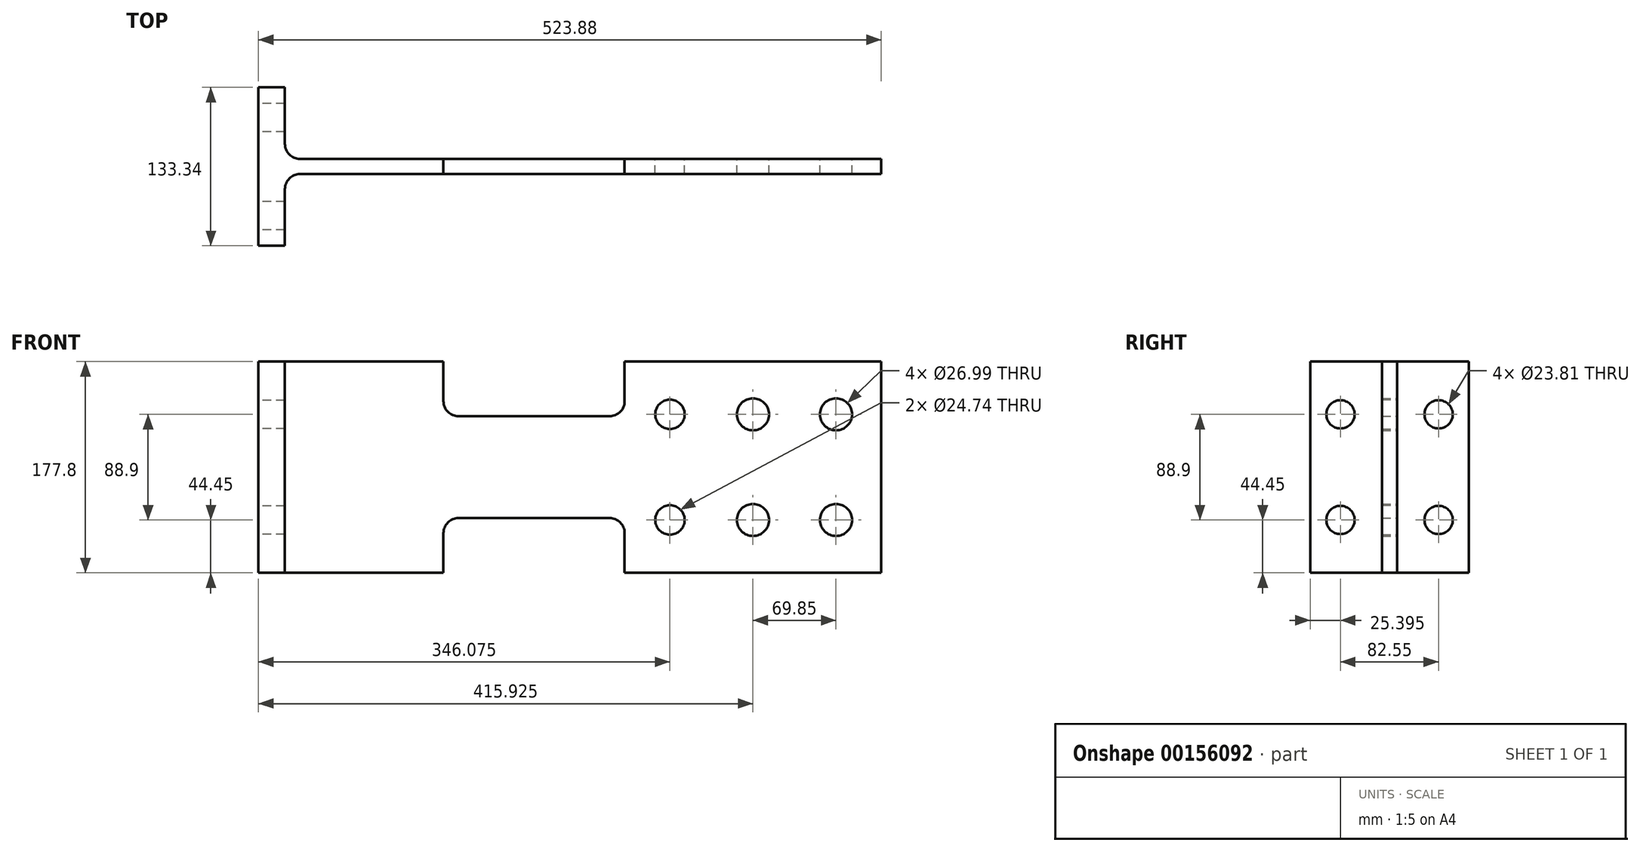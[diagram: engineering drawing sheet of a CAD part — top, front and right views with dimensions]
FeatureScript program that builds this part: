
annotation { "Feature Type Name" : "Feature", "Feature Type Description" : "" }
export const myFeature = defineFeature(function(context is Context, id is Id, definition is map)
    precondition{}
    {
        {
            var Q0;
            Q0=qCreatedBy(makeId("Front.planeOp"),FACE);
            var sketch = newSketch(context, id + "F0", { "sketchPlane" : qUnion([Q0])});
            skLineSegment(sketch, "E0", {"start": v(0, 0) * mm, "end": v(0, 88.9) * mm});
            skLineSegment(sketch, "E1", {"start": v(0, 88.9) * mm, "end": v(155.57, 88.9) * mm});
            skLineSegment(sketch, "E2", {"start": v(523.88, 88.9) * mm, "end": v(523.88, 0) * mm});
            skPoint(sketch, "E3", {"position": v(485.78, 44.45) * mm});
            skPoint(sketch, "E4", {"position": v(415.93, 44.45) * mm});
            skPoint(sketch, "E5", {"position": v(346.08, 44.45) * mm});
            skLineSegment(sketch, "E6", {"start": v(307.98, 88.9) * mm, "end": v(307.98, 55.56) * mm});
            skLineSegment(sketch, "E7", {"start": v(155.57, 88.9) * mm, "end": v(155.57, 55.56) * mm});
            skLineSegment(sketch, "E8", {"start": v(168.27, 42.86) * mm, "end": v(295.28, 42.86) * mm});
            skPoint(sketch, "E9.newPointA", {"position": v(155.57, 44.45) * mm});
            skArc(sketch, "E9.filletArc", {"start": v(155.57, 55.56) * mm, "mid": v(159.3, 46.58) * mm, "end": v(168.27, 42.86) * mm});
            skPoint(sketch, "E10.newPointA", {"position": v(307.98, 42.86) * mm});
            skPoint(sketch, "E10.newPointB", {"position": v(307.98, 44.45) * mm});
            skArc(sketch, "E10.filletArc", {"start": v(295.28, 42.86) * mm, "mid": v(304.26, 46.58) * mm, "end": v(307.98, 55.56) * mm});
            skCircle(sketch, "E11", {"center": v(346.08, 44.45) * mm, "radius": 12.37 * mm});
            skCircle(sketch, "E12", {"center": v(415.93, 44.45) * mm, "radius": 13.5 * mm});
            skCircle(sketch, "E13", {"center": v(485.78, 44.45) * mm, "radius": 13.5 * mm});
            skLineSegment(sketch, "E14.trimOffspring", {"start": v(307.98, 88.9) * mm, "end": v(523.88, 88.9) * mm});
            skArc(sketch, "E15.MirrorCS", {"start": v(155.57, -55.56) * mm, "mid": v(159.3, -46.58) * mm, "end": v(168.27, -42.86) * mm});
            skArc(sketch, "E16.MirrorCS", {"start": v(295.28, -42.86) * mm, "mid": v(304.26, -46.58) * mm, "end": v(307.98, -55.56) * mm});
            skPoint(sketch, "E17.MirrorP", {"position": v(307.98, -44.45) * mm});
            skPoint(sketch, "E18.MirrorP", {"position": v(307.98, -42.86) * mm});
            skLineSegment(sketch, "E19.MirrorCS", {"start": v(0, 0) * mm, "end": v(0, -88.9) * mm});
            skLineSegment(sketch, "E20.MirrorCS", {"start": v(0, -88.9) * mm, "end": v(155.57, -88.9) * mm});
            skLineSegment(sketch, "E21.MirrorCS", {"start": v(307.98, -88.9) * mm, "end": v(523.88, -88.9) * mm});
            skCircle(sketch, "E22.MirrorC", {"center": v(485.78, -44.45) * mm, "radius": 13.5 * mm});
            skLineSegment(sketch, "E23.MirrorCS", {"start": v(168.27, -42.86) * mm, "end": v(295.28, -42.86) * mm});
            skLineSegment(sketch, "E24.MirrorCS", {"start": v(523.88, -88.9) * mm, "end": v(523.88, 0) * mm});
            skPoint(sketch, "E25.MirrorP", {"position": v(155.57, -44.45) * mm});
            skCircle(sketch, "E26.MirrorC", {"center": v(346.08, -44.45) * mm, "radius": 12.37 * mm});
            skCircle(sketch, "E27.MirrorC", {"center": v(415.93, -44.45) * mm, "radius": 13.5 * mm});
            skLineSegment(sketch, "E28.MirrorCS", {"start": v(155.57, -88.9) * mm, "end": v(155.57, -55.56) * mm});
            skLineSegment(sketch, "E29.MirrorCS", {"start": v(307.98, -88.9) * mm, "end": v(307.98, -55.56) * mm});
            skSolve(sketch);
        }
        {
            var Q0;
            Q0=makeQuery(id+"F0.imprint","IMPRINT",FACE,{"disambiguationData":[TD([[makeQuery(id+"F0.imprint","IMPRINT",EDGE,{"derivedFrom":sQuery(id+"F0.wireOp",EDGE,"E0")}),-1.0]])]});
            extrude(context, id + "F1", {"entities" : qUnion([Q0]), "depth" : 6.35 * mm});
        }
        {
            var Q0;
            Q0=makeQuery(id+"F1.opExtrude","CAP_FACE",FACE,{"disambiguationData":[OSD([sQuery(id+"F0.wireOp",EDGE,"E0"),sQuery(id+"F0.wireOp",EDGE,"E1"),sQuery(id+"F0.wireOp",EDGE,"E2"),sQuery(id+"F0.wireOp",EDGE,"E6"),sQuery(id+"F0.wireOp",EDGE,"E7"),sQuery(id+"F0.wireOp",EDGE,"E8"),sQuery(id+"F0.wireOp",EDGE,"E9.filletArc"),sQuery(id+"F0.wireOp",EDGE,"E10.filletArc"),sQuery(id+"F0.wireOp",EDGE,"E11"),sQuery(id+"F0.wireOp",EDGE,"E12"),sQuery(id+"F0.wireOp",EDGE,"E13"),sQuery(id+"F0.wireOp",EDGE,"E14.trimOffspring"),sQuery(id+"F0.wireOp",EDGE,"E15.MirrorCS"),sQuery(id+"F0.wireOp",EDGE,"E16.MirrorCS"),sQuery(id+"F0.wireOp",EDGE,"E19.MirrorCS"),sQuery(id+"F0.wireOp",EDGE,"E20.MirrorCS"),sQuery(id+"F0.wireOp",EDGE,"E21.MirrorCS"),sQuery(id+"F0.wireOp",EDGE,"E22.MirrorC"),sQuery(id+"F0.wireOp",EDGE,"E23.MirrorCS"),sQuery(id+"F0.wireOp",EDGE,"E24.MirrorCS"),sQuery(id+"F0.wireOp",EDGE,"E26.MirrorC"),sQuery(id+"F0.wireOp",EDGE,"E27.MirrorC"),sQuery(id+"F0.wireOp",EDGE,"E28.MirrorCS"),sQuery(id+"F0.wireOp",EDGE,"E29.MirrorCS")])],"isStart":true});
            extrude(context, id + "F2", {"entities" : qUnion([Q0]), "operationType" : NewBodyOperationType.ADD, "depth" : 6.35 * mm});
        }
        {
            var Q0;
            Q0=qCreatedBy(makeId("Right.planeOp"),FACE);
            var sketch = newSketch(context, id + "F3", { "sketchPlane" : qUnion([Q0])});
            skLineSegment(sketch, "E30", {"start": v(0, 88.9) * mm, "end": v(-66.68, 88.9) * mm});
            skLineSegment(sketch, "E31", {"start": v(-66.68, 88.9) * mm, "end": v(-66.68, 0) * mm});
            skPoint(sketch, "E32", {"position": v(-66.68, 44.45) * mm});
            skPoint(sketch, "E33", {"position": v(-41.28, 44.45) * mm});
            skCircle(sketch, "E34", {"center": v(-41.28, 44.45) * mm, "radius": 11.9 * mm});
            skLineSegment(sketch, "E35.MirrorCS", {"start": v(0, 88.9) * mm, "end": v(66.68, 88.9) * mm});
            skLineSegment(sketch, "E36.MirrorCS", {"start": v(66.68, 88.9) * mm, "end": v(66.68, 0) * mm});
            skPoint(sketch, "E37.MirrorP", {"position": v(41.28, 44.45) * mm});
            skPoint(sketch, "E38.MirrorP", {"position": v(66.68, 44.45) * mm});
            skCircle(sketch, "E39.MirrorC", {"center": v(41.28, 44.45) * mm, "radius": 11.9 * mm});
            skCircle(sketch, "E40.MirrorC", {"center": v(41.28, -44.45) * mm, "radius": 11.9 * mm});
            skLineSegment(sketch, "E41.MirrorCS", {"start": v(66.68, -88.9) * mm, "end": v(66.68, 0) * mm});
            skLineSegment(sketch, "E42.MirrorCS", {"start": v(0, -88.9) * mm, "end": v(66.68, -88.9) * mm});
            skCircle(sketch, "E43.MirrorC", {"center": v(-41.28, -44.45) * mm, "radius": 11.9 * mm});
            skLineSegment(sketch, "E44.MirrorCS", {"start": v(0, -88.9) * mm, "end": v(-66.68, -88.9) * mm});
            skLineSegment(sketch, "E45.MirrorCS", {"start": v(-66.68, -88.9) * mm, "end": v(-66.68, 0) * mm});
            skPoint(sketch, "E46.MirrorP", {"position": v(66.68, -44.45) * mm});
            skPoint(sketch, "E47.MirrorP", {"position": v(-66.68, -44.45) * mm});
            skSolve(sketch);
        }
        {
            var Q0;
            Q0=makeQuery(id+"F3.imprint","IMPRINT",FACE,{"disambiguationData":[TD([[makeQuery(id+"F3.imprint","IMPRINT",EDGE,{"derivedFrom":sQuery(id+"F3.wireOp",EDGE,"E30")}),1.0]])]});
            extrude(context, id + "F4", {"entities" : qUnion([Q0]), "operationType" : NewBodyOperationType.ADD, "depth" : 22.22 * mm});
        }
        {
            var Q0;
            Q0=makeQuery(id+"F4.boolean.opBoolean","INTERSECT",EDGE,{"derivedFrom":[makeQuery(id+"F2.opExtrude","CAP_FACE",FACE,{"disambiguationData":[OSD([sQuery(id+"F0.wireOp",EDGE,"E0"),sQuery(id+"F0.wireOp",EDGE,"E1"),sQuery(id+"F0.wireOp",EDGE,"E2"),sQuery(id+"F0.wireOp",EDGE,"E6"),sQuery(id+"F0.wireOp",EDGE,"E7"),sQuery(id+"F0.wireOp",EDGE,"E8"),sQuery(id+"F0.wireOp",EDGE,"E9.filletArc"),sQuery(id+"F0.wireOp",EDGE,"E10.filletArc"),sQuery(id+"F0.wireOp",EDGE,"E11"),sQuery(id+"F0.wireOp",EDGE,"E12"),sQuery(id+"F0.wireOp",EDGE,"E13"),sQuery(id+"F0.wireOp",EDGE,"E14.trimOffspring"),sQuery(id+"F0.wireOp",EDGE,"E15.MirrorCS"),sQuery(id+"F0.wireOp",EDGE,"E16.MirrorCS"),sQuery(id+"F0.wireOp",EDGE,"E19.MirrorCS"),sQuery(id+"F0.wireOp",EDGE,"E20.MirrorCS"),sQuery(id+"F0.wireOp",EDGE,"E21.MirrorCS"),sQuery(id+"F0.wireOp",EDGE,"E22.MirrorC"),sQuery(id+"F0.wireOp",EDGE,"E23.MirrorCS"),sQuery(id+"F0.wireOp",EDGE,"E24.MirrorCS"),sQuery(id+"F0.wireOp",EDGE,"E26.MirrorC"),sQuery(id+"F0.wireOp",EDGE,"E27.MirrorC"),sQuery(id+"F0.wireOp",EDGE,"E28.MirrorCS"),sQuery(id+"F0.wireOp",EDGE,"E29.MirrorCS")])],"isStart":false}),makeQuery(id+"F4.opExtrude","CAP_FACE",FACE,{"disambiguationData":[OSD([sQuery(id+"F3.wireOp",EDGE,"E30"),sQuery(id+"F3.wireOp",EDGE,"E31"),sQuery(id+"F3.wireOp",EDGE,"E34"),sQuery(id+"F3.wireOp",EDGE,"E35.MirrorCS"),sQuery(id+"F3.wireOp",EDGE,"E36.MirrorCS"),sQuery(id+"F3.wireOp",EDGE,"E39.MirrorC"),sQuery(id+"F3.wireOp",EDGE,"E40.MirrorC"),sQuery(id+"F3.wireOp",EDGE,"E41.MirrorCS"),sQuery(id+"F3.wireOp",EDGE,"E42.MirrorCS"),sQuery(id+"F3.wireOp",EDGE,"E43.MirrorC"),sQuery(id+"F3.wireOp",EDGE,"E44.MirrorCS"),sQuery(id+"F3.wireOp",EDGE,"E45.MirrorCS")])],"isStart":false})]});
            var Q1;
            Q1=makeQuery(id+"F4.boolean.opBoolean","INTERSECT",EDGE,{"derivedFrom":[makeQuery(id+"F1.opExtrude","CAP_FACE",FACE,{"disambiguationData":[OSD([sQuery(id+"F0.wireOp",EDGE,"E0"),sQuery(id+"F0.wireOp",EDGE,"E1"),sQuery(id+"F0.wireOp",EDGE,"E2"),sQuery(id+"F0.wireOp",EDGE,"E6"),sQuery(id+"F0.wireOp",EDGE,"E7"),sQuery(id+"F0.wireOp",EDGE,"E8"),sQuery(id+"F0.wireOp",EDGE,"E9.filletArc"),sQuery(id+"F0.wireOp",EDGE,"E10.filletArc"),sQuery(id+"F0.wireOp",EDGE,"E11"),sQuery(id+"F0.wireOp",EDGE,"E12"),sQuery(id+"F0.wireOp",EDGE,"E13"),sQuery(id+"F0.wireOp",EDGE,"E14.trimOffspring"),sQuery(id+"F0.wireOp",EDGE,"E15.MirrorCS"),sQuery(id+"F0.wireOp",EDGE,"E16.MirrorCS"),sQuery(id+"F0.wireOp",EDGE,"E19.MirrorCS"),sQuery(id+"F0.wireOp",EDGE,"E20.MirrorCS"),sQuery(id+"F0.wireOp",EDGE,"E21.MirrorCS"),sQuery(id+"F0.wireOp",EDGE,"E22.MirrorC"),sQuery(id+"F0.wireOp",EDGE,"E23.MirrorCS"),sQuery(id+"F0.wireOp",EDGE,"E24.MirrorCS"),sQuery(id+"F0.wireOp",EDGE,"E26.MirrorC"),sQuery(id+"F0.wireOp",EDGE,"E27.MirrorC"),sQuery(id+"F0.wireOp",EDGE,"E28.MirrorCS"),sQuery(id+"F0.wireOp",EDGE,"E29.MirrorCS")])],"isStart":false}),makeQuery(id+"F4.opExtrude","CAP_FACE",FACE,{"disambiguationData":[OSD([sQuery(id+"F3.wireOp",EDGE,"E30"),sQuery(id+"F3.wireOp",EDGE,"E31"),sQuery(id+"F3.wireOp",EDGE,"E34"),sQuery(id+"F3.wireOp",EDGE,"E35.MirrorCS"),sQuery(id+"F3.wireOp",EDGE,"E36.MirrorCS"),sQuery(id+"F3.wireOp",EDGE,"E39.MirrorC"),sQuery(id+"F3.wireOp",EDGE,"E40.MirrorC"),sQuery(id+"F3.wireOp",EDGE,"E41.MirrorCS"),sQuery(id+"F3.wireOp",EDGE,"E42.MirrorCS"),sQuery(id+"F3.wireOp",EDGE,"E43.MirrorC"),sQuery(id+"F3.wireOp",EDGE,"E44.MirrorCS"),sQuery(id+"F3.wireOp",EDGE,"E45.MirrorCS")])],"isStart":false})]});
            fillet(context, id + "F5", {"entities" : qUnion([Q0, Q1]), "radius" : 12.7 * mm, "tangentPropagation" : true, "allowEdgeOverflow" : false});
        }
    });
